# Revit family: ЭВАН PRACTIC 36-120 кВт
name_source: partatom
category: Оборудование
units: mm (PartAtom-declared; Revit-internal decimal feet)

## family parameters
Всегда вертикально = Да
Классификация = Нет
На основе рабочей плоскости = Да
Общий = Нет
При загрузке вырезать с полостями = Нет
Размер круглого соединителя = Использовать диаметр
Тип детали = Нормальный
Точка расчета площади = Нет

## types (9) — shared parameters
ADSK_Классификация нагрузок = Прочее
ADSK_Количество фаз = 3
ADSK_Материал = Сталь
ADSK_Размер_Высота = 794 мм
ADSK_Размер_Длина = 448 мм
ADSK_Размер_Ширина = 288 мм
ADSK_Расход теплоносителя = 0.0 м³/ч
Dn = 32 мм
База = ЭЛЕКТРИЧЕСКИЙ ТЕПЛОГЕНЕРАТОР (КОТЕЛ)
Диапазон регулируемых температур теплоносителя, оС = От +10 до +85
Максимальная температура теплоносителя, оС = +85
Материал корпуса = Сталь
Минимальная температура теплоносителя, оС = +10
Объем колбы котла, л = 19,3
Рабочее давление, МПа = 0,07-0,32
Резьба патрубков для подключения трубопроводов теплоносителя = G1 1/4
zero-valued in all types: Отметка по умолчанию

## per-type parameters (varying)
| type | ADSK_Номинальная мощность | Потребляемая электрическая мощность при максимальной тепловой мощность  в час, кВт/ч |
| ЭВАН PRACTIC 36 кВт | 36000 Вт | 37.8 |
| ЭВАН PRACTIC 42 кВт | 42000 Вт | 44.1 |
| ЭВАН PRACTIC 50 кВт | 50000 Вт | 52.5 |
| ЭВАН PRACTIC 60 кВт | 60000 Вт | 63 |
| ЭВАН PRACTIC 72 кВт | 72000 Вт | 75.6 |
| ЭВАН PRACTIC 84 кВт | 84000 Вт | 88.2 |
| ЭВАН PRACTIC 90 кВт | 90000 Вт | 94.5 |
| ЭВАН PRACTIC 105 кВт | 105000 Вт | 110.3 |
| ЭВАН PRACTIC 120 кВт | 120000 Вт | 126 |
